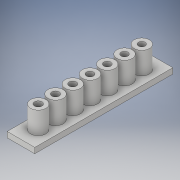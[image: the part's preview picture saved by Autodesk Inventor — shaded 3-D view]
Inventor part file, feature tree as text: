
AUTODESK INVENTOR PART (.ipt)
format: ipt  version: 2019 (Build 230136000, 136)  size: 163,328 bytes
history: native  units: mm
features: extrude x3, sketch x3, projected_geometry x1
ambient origin geometry x8: Origin, YZ Plane, XZ Plane, XY Plane, X Axis, Y Axis, Z Axis, Center Point
bodies: Solid1 (feature_tree)
feature tree (7):
  extrude  "Extrusion1"  Depth=50.0mm
  sketch  "Sketch2"  dims[d2=2.0mm d3=0.0mm d4=2.4mm]
  extrude  "Extrusion2"  Depth=2.0mm
  extrude  "Extrusion3"  Depth=8.0mm
  sketch  "Sketch1"  dims[d0=10.0mm d1=50.0mm]
  sketch  "Sketch3"  dims[d5=6.25mm d6=2.45mm d7=2.5mm d8=2.55mm d9=2.6mm d10=2.65mm d11=2.7mm d12=6.25mm d13=6.25mm d14=6.25mm d15=6.25mm d17=6.25mm d18=6.25mm d19=6.25mm d20=5.5mm d21=70.0mm d23=6.25mm d24=10.0mm d26=10.0mm d28=8.0mm d29=0.0mm d30=8.0mm d31=0.0mm]
  projected_geometry  "Projected Loop1"
